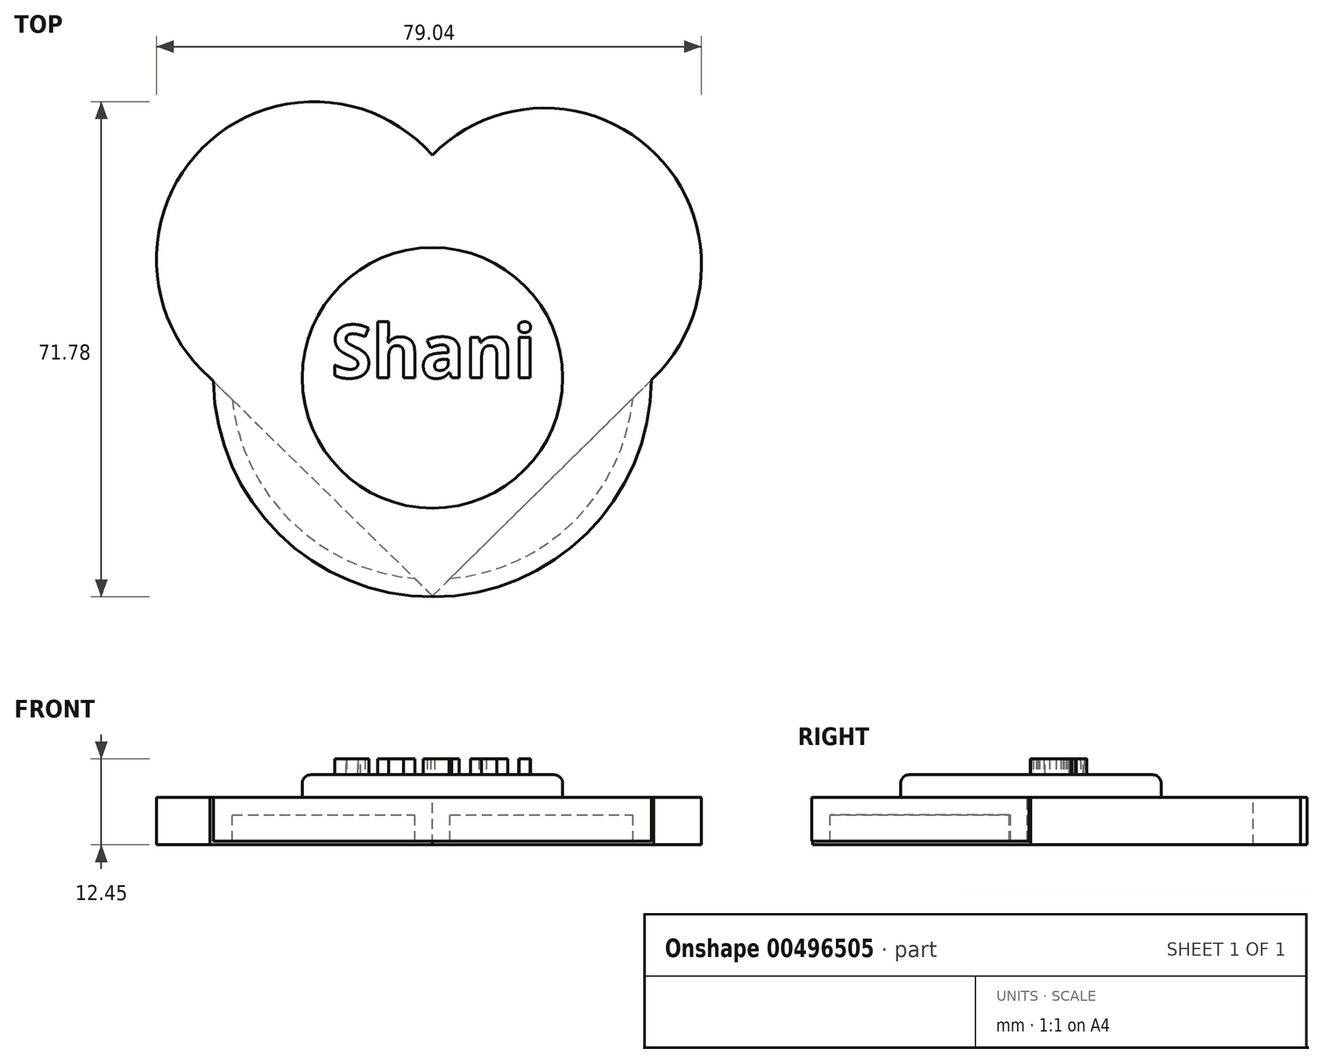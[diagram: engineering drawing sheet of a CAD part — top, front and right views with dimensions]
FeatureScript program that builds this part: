
annotation { "Feature Type Name" : "Feature", "Feature Type Description" : "" }
export const myFeature = defineFeature(function(context is Context, id is Id, definition is map)
    precondition{}
    {
        {
            var Q0;
            Q0=qCreatedBy(makeId("Top.planeOp"),FACE);
            var sketch = newSketch(context, id + "F0", { "sketchPlane" : qUnion([Q0])});
            skCircle(sketch, "E0", {"center": v(0, 0) * mm, "radius": 31.75 * mm});
            skSolve(sketch);
        }
        {
            var Q0;
            Q0=makeQuery(id+"F0.imprint","IMPRINT",FACE,{"disambiguationData":[TD([[makeQuery(id+"F0.imprint","IMPRINT",EDGE,{"derivedFrom":sQuery(id+"F0.wireOp",EDGE,"E0")}),1.0]])]});
            extrude(context, id + "F1", {"entities" : qUnion([Q0]), "oppositeDirection" : true, "depth" : 6.35 * mm});
        }
        {
            var Q0;
            Q0=makeQuery(id+"F1.opExtrude","CAP_FACE",FACE,{"disambiguationData":[OSD([sQuery(id+"F0.wireOp",EDGE,"E0")])],"isStart":false});
            shell(context, id + "F2", {"entities" : qUnion([Q0]), "thickness" : 2.54 * mm});
        }
        {
            var Q0;
            Q0=makeQuery(id+"F1.opExtrude","CAP_FACE",FACE,{"disambiguationData":[OSD([sQuery(id+"F0.wireOp",EDGE,"E0")])],"isStart":true});
            var sketch = newSketch(context, id + "F3", { "sketchPlane" : qUnion([Q0])});
            skCircle(sketch, "E1", {"center": v(0, 0) * mm, "radius": 18.88 * mm});
            skSolve(sketch);
        }
        {
            var Q0;
            Q0=makeQuery(id+"F3.imprint","IMPRINT",FACE,{"disambiguationData":[TD([[makeQuery(id+"F3.imprint","IMPRINT",EDGE,{"derivedFrom":sQuery(id+"F3.wireOp",EDGE,"E1")}),1.0]])]});
            extrude(context, id + "F4", {"entities" : qUnion([Q0]), "operationType" : NewBodyOperationType.ADD, "depth" : 3.3 * mm});
        }
        {
            var Q0;
            Q0=makeQuery(id+"F4.opExtrude","CAP_FACE",FACE,{"disambiguationData":[OSD([sQuery(id+"F3.wireOp",EDGE,"E1")])],"isStart":false});
            var sketch = newSketch(context, id + "F5", { "sketchPlane" : qUnion([Q0])});
            skText(sketch, "E2", { "text": "Shani", "fontName": "OpenSans-Bold.ttf"});
            const initialGuessF5  = {"E2": [-0.01469, 0, 1, 0, 0.0077]};
            skSetInitialGuess(sketch, initialGuessF5);
            skSolve(sketch);
        }
        {
            var Q0;
            Q0 = qSketchRegion(id + "F5", true);
            extrude(context, id + "F6", {"entities" : qUnion([Q0]), "operationType" : NewBodyOperationType.ADD, "depth" : 2.3 * mm});
        }
        {
            var Q0;
            Q0=makeQuery(id+"F4.opExtrude","CAP_EDGE",EDGE,{"disambiguationData":[OSD([sQuery(id+"F3.wireOp",EDGE,"E1")])],"isStart":false});
            fillet(context, id + "F7", {"entities" : qUnion([Q0]), "radius" : 1.27 * mm, "tangentPropagation" : true, "allowEdgeOverflow" : false});
        }
        {
            var Q0;
            Q0=qCreatedBy(makeId("Top.planeOp"),FACE);
            var sketch = newSketch(context, id + "F8", { "sketchPlane" : qUnion([Q0])});
            skArc(sketch, "E3", {"start": v(32.05, 0) * mm, "mid": v(32.4, 32.4) * mm, "end": v(0, 32.26) * mm});
            skArc(sketch, "E4", {"start": v(0, 32.26) * mm, "mid": v(-33.34, 33.34) * mm, "end": v(-32.26, 0) * mm});
            skLineSegment(sketch, "E5", {"start": v(-32.26, 0) * mm, "end": v(0, -31.62) * mm});
            skLineSegment(sketch, "E6", {"start": v(0, -31.62) * mm, "end": v(32.05, 0) * mm});
            skSolve(sketch);
        }
        {
            var Q0;
            Q0=makeQuery(id+"F8.imprint","IMPRINT",FACE,{"disambiguationData":[TD([[makeQuery(id+"F8.imprint","IMPRINT",EDGE,{"derivedFrom":sQuery(id+"F8.wireOp",EDGE,"E3")}),1.0]])]});
            extrude(context, id + "F9", {"entities" : qUnion([Q0]), "operationType" : NewBodyOperationType.ADD, "oppositeDirection" : true, "depth" : 6.86 * mm});
        }
    });
